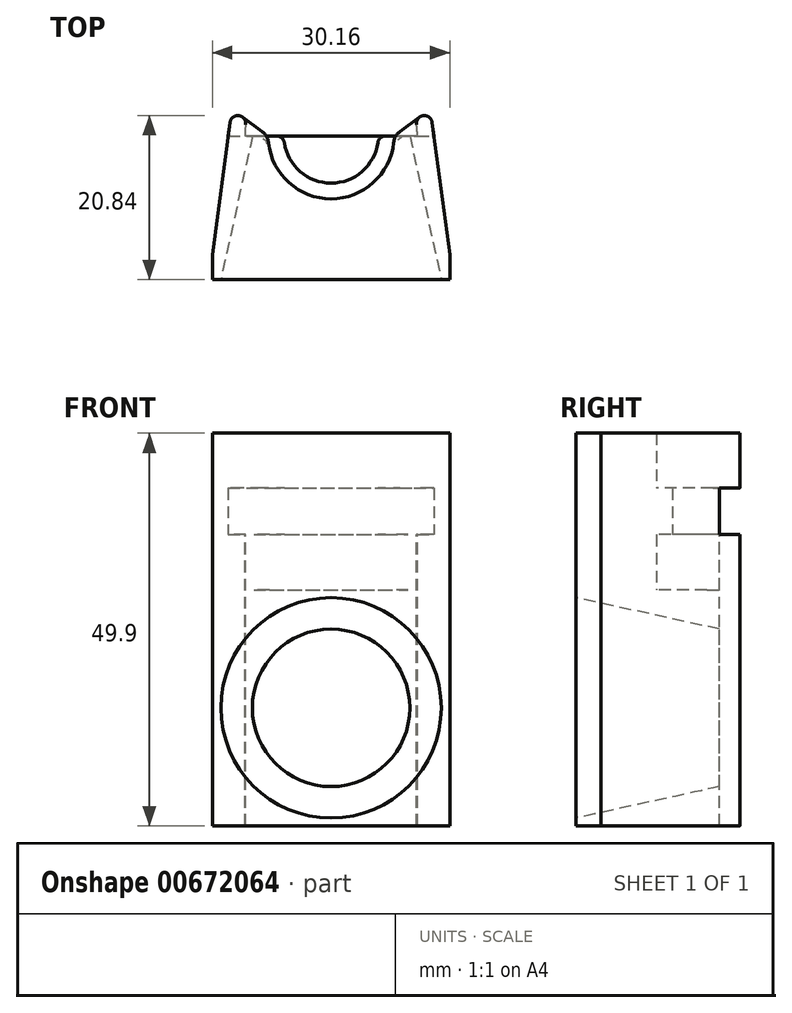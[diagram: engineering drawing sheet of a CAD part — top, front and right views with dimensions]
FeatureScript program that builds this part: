
annotation { "Feature Type Name" : "Feature", "Feature Type Description" : "" }
export const myFeature = defineFeature(function(context is Context, id is Id, definition is map)
    precondition{}
    {
        {
            var Q0;
            Q0=qCreatedBy(makeId("Top.planeOp"),FACE);
            var sketch = newSketch(context, id + "F0", { "sketchPlane" : qUnion([Q0])});
            skLineSegment(sketch, "E0.bottom", {"start": v(25.4, -25.4) * mm, "end": v(-25.4, -25.4) * mm});
            skLineSegment(sketch, "E0.top", {"start": v(25.4, 25.4) * mm, "end": v(-25.4, 25.4) * mm});
            skLineSegment(sketch, "E0.left", {"start": v(25.4, -25.4) * mm, "end": v(25.4, 25.4) * mm});
            skLineSegment(sketch, "E0.right", {"start": v(-25.4, -25.4) * mm, "end": v(-25.4, 25.4) * mm});
            skPoint(sketch, "E0.middle", {"position": v(0, 0) * mm});
            skSolve(sketch);
        }
        {
            var Q0;
            Q0 = qSketchRegion(id + "F0", true);
            extrude(context, id + "F1", {"entities" : qUnion([Q0]), "depth" : 30 * mm, "offsetDistance" : 25.4 * mm});
        }
        {
            var Q0;
            Q0=makeQuery(id+"F1.opExtrude","CAP_FACE",FACE,{"disambiguationData":[OSD([sQuery(id+"F0.wireOp",EDGE,"E0.bottom"),sQuery(id+"F0.wireOp",EDGE,"E0.top"),sQuery(id+"F0.wireOp",EDGE,"E0.left"),sQuery(id+"F0.wireOp",EDGE,"E0.right")])],"isStart":false});
            var sketch = newSketch(context, id + "F2", { "sketchPlane" : qUnion([Q0])});
            skArc(sketch, "E1", {"start": v(-10.86, 1.45) * mm, "mid": v(0, -10.95) * mm, "end": v(10.86, 1.45) * mm});
            skLineSegment(sketch, "E2.bottom", {"start": v(15.08, -15.08) * mm, "end": v(-15.08, -15.08) * mm});
            skLineSegment(sketch, "E3", {"start": v(-10.95, 0) * mm, "end": v(12.95, 0) * mm});
            skPoint(sketch, "E2.top.end.orphan", {"position": v(-15.08, 15.08) * mm});
            skPoint(sketch, "E4.orphan", {"position": v(15.08, 15.08) * mm});
            skPoint(sketch, "E5.orphan", {"position": v(15.08, 0) * mm});
            skPoint(sketch, "E2.right.end.orphan", {"position": v(-15.08, 0) * mm});
            skLineSegment(sketch, "E6.0", {"start": v(15.08, -18.26) * mm, "end": v(-15.08, -18.26) * mm});
            skLineSegment(sketch, "E7", {"start": v(-15.08, -15.08) * mm, "end": v(-15.08, -18.26) * mm});
            skLineSegment(sketch, "E8", {"start": v(15.08, -15.08) * mm, "end": v(15.08, -18.26) * mm});
            skLineSegment(sketch, "E9", {"start": v(15.08, -15.08) * mm, "end": v(12.84, 1.71) * mm});
            skLineSegment(sketch, "E10", {"start": v(-15.08, -15.08) * mm, "end": v(-12.84, 1.71) * mm});
            skArc(sketch, "E11", {"start": v(12.84, 1.71) * mm, "mid": v(11.72, 2.57) * mm, "end": v(10.86, 1.45) * mm});
            skArc(sketch, "E12", {"start": v(-10.86, 1.45) * mm, "mid": v(-11.72, 2.57) * mm, "end": v(-12.84, 1.71) * mm});
            skSolve(sketch);
        }
        {
            var Q0;
            Q0=makeQuery(id+"F2.imprint","IMPRINT",FACE,{"disambiguationData":[TD([[makeQuery(id+"F2.imprint","IMPRINT",EDGE,{"derivedFrom":sQuery(id+"F2.wireOp",EDGE,"E6.0")}),1.0]])]});
            var Q1;
            {var subQ0=sQuery(id+"F2.wireOp",EDGE,"E3");var subQ1=sQuery(id+"F2.wireOp",EDGE,"E1");var subQ2=makeQuery(id+"F2.imprint","INTERSECT",VERTEX,{"disambiguationData":[OD(0.0)],"derivedFrom":[subQ1,subQ0]});Q1=makeQuery(id+"F2.imprint","IMPRINT",FACE,{"disambiguationData":[TD([[makeQuery(id+"F2.imprint","IMPRINT",EDGE,{"disambiguationData":[TD([[subQ2,-1.0]])],"derivedFrom":subQ1}),1.0]])]});}
            var Q2;
            Q2=makeQuery(id+"F1.opExtrude","CAP_FACE",FACE,{"disambiguationData":[OSD([sQuery(id+"F0.wireOp",EDGE,"E0.bottom"),sQuery(id+"F0.wireOp",EDGE,"E0.top"),sQuery(id+"F0.wireOp",EDGE,"E0.left"),sQuery(id+"F0.wireOp",EDGE,"E0.right")])],"isStart":true});
            extrude(context, id + "F3", {"entities" : qUnion([Q0, Q1]), "operationType" : NewBodyOperationType.REMOVE, "endBound" : BoundingType.UP_TO_SURFACE, "oppositeDirection" : true, "depth" : 25.4 * mm, "endBoundEntityFace" : qUnion([Q2]), "offsetDistance" : 25.4 * mm});
        }
        {
            var Q0;
            Q0=makeQuery(id+"F3.boolean.opBoolean","COPY",FACE,{"derivedFrom":makeQuery(id+"F3.opExtrude","SWEPT_FACE",FACE,{"disambiguationData":[OSD([sQuery(id+"F2.wireOp",EDGE,"E6.0")])]})});
            var sketch = newSketch(context, id + "F4", { "sketchPlane" : qUnion([Q0])});
            skCircle(sketch, "E13", {"center": v(0, 15) * mm, "radius": 14 * mm});
            skSolve(sketch);
        }
        {
            var Q0;
            Q0=qCreatedBy(makeId("Front.planeOp"),FACE);
            var sketch = newSketch(context, id + "F5", { "sketchPlane" : qUnion([Q0])});
            skCircle(sketch, "E14", {"center": v(0, 15) * mm, "radius": 10 * mm});
            skSolve(sketch);
        }
        {
            var Q1;
            Q1=makeQuery(id+"F5.imprint","IMPRINT",FACE,{"disambiguationData":[TD([[makeQuery(id+"F5.imprint","IMPRINT",EDGE,{"derivedFrom":sQuery(id+"F5.wireOp",EDGE,"E14")}),1.0]])]});
            var Q2;
            Q2=makeQuery(id+"F4.imprint","IMPRINT",FACE,{"disambiguationData":[TD([[makeQuery(id+"F4.imprint","IMPRINT",EDGE,{"derivedFrom":sQuery(id+"F4.wireOp",EDGE,"E13")}),1.0]])]});
            var Q3;
            Q3=makeQuery(id+"F5.imprint","IMPRINT",FACE,{"disambiguationData":[TD([[makeQuery(id+"F5.imprint","IMPRINT",EDGE,{"derivedFrom":sQuery(id+"F5.wireOp",EDGE,"E14")}),1.0]])]});
            var Q4;
            Q4=makeQuery(id+"F4.imprint","IMPRINT",FACE,{"disambiguationData":[TD([[makeQuery(id+"F4.imprint","IMPRINT",EDGE,{"derivedFrom":sQuery(id+"F4.wireOp",EDGE,"E13")}),1.0]])]});
            loft(context, id + "F6", {"operationType" : NewBodyOperationType.REMOVE, "sheetProfilesArray" : [{ "sheetProfileEntities" : qUnion([Q1]) }, { "sheetProfileEntities" : qUnion([Q2]) }], "wireProfilesArray" : [{ "wireProfileEntities" : qUnion([Q3]) }, { "wireProfileEntities" : qUnion([Q4]) }]});
        }
        {
            var Q0;
            Q0=makeQuery(id+"F1.opExtrude","CAP_FACE",FACE,{"disambiguationData":[OSD([sQuery(id+"F0.wireOp",EDGE,"E0.bottom"),sQuery(id+"F0.wireOp",EDGE,"E0.top"),sQuery(id+"F0.wireOp",EDGE,"E0.left"),sQuery(id+"F0.wireOp",EDGE,"E0.right")])],"isStart":false});
            var sketch = newSketch(context, id + "F7", { "sketchPlane" : qUnion([Q0])});
            skArc(sketch, "E15", {"start": v(-8, 0) * mm, "mid": v(0, -8) * mm, "end": v(8, 0) * mm});
            skLineSegment(sketch, "E16", {"start": v(-8, 0) * mm, "end": v(-11.26, 2.39) * mm});
            skLineSegment(sketch, "E17", {"start": v(8, 0) * mm, "end": v(11.26, 2.39) * mm});
            skSolve(sketch);
        }
        {
            var Q0;
            {var subQ0=makeQuery(id+"F3.boolean.opBoolean","COPY",EDGE,{"derivedFrom":makeQuery(id+"F3.opExtrude","CAP_EDGE",EDGE,{"disambiguationData":[OSD([sQuery(id+"F2.wireOp",EDGE,"E1")])],"isStart":true})});Q0=makeQuery(id+"F7.imprint","IMPRINT",FACE,{"disambiguationData":[TD([[makeQuery(id+"F7.imprint","IMPRINT",EDGE,{"derivedFrom":subQ0}),-1.0]])]});}
            var Q1;
            Q1=makeQuery(id+"F7.imprint","IMPRINT",FACE,{"disambiguationData":[TD([[makeQuery(id+"F7.imprint","IMPRINT",EDGE,{"derivedFrom":sQuery(id+"F7.wireOp",EDGE,"E15")}),-1.0]])]});
            extrude(context, id + "F8", {"entities" : qUnion([Q0, Q1]), "operationType" : NewBodyOperationType.ADD, "depth" : 7 * mm, "offsetDistance" : 25.4 * mm});
        }
        {
            var Q0;
            Q0=makeQuery(id+"F8.opExtrude","CAP_FACE",FACE,{"disambiguationData":[OSD([sQuery(id+"F2.wireOp",EDGE,"E6.0"),sQuery(id+"F2.wireOp",EDGE,"E7"),sQuery(id+"F2.wireOp",EDGE,"E8"),sQuery(id+"F2.wireOp",EDGE,"E9"),sQuery(id+"F2.wireOp",EDGE,"E10"),sQuery(id+"F2.wireOp",EDGE,"E11"),sQuery(id+"F2.wireOp",EDGE,"E12"),sQuery(id+"F7.wireOp",EDGE,"E15"),sQuery(id+"F7.wireOp",EDGE,"E16"),sQuery(id+"F7.wireOp",EDGE,"E17")])],"isStart":false});
            var sketch = newSketch(context, id + "F9", { "sketchPlane" : qUnion([Q0])});
            skArc(sketch, "E18", {"start": v(-6, 0) * mm, "mid": v(0, -6) * mm, "end": v(6, 0) * mm});
            skLineSegment(sketch, "E19", {"start": v(-6, 0) * mm, "end": v(6, 0) * mm});
            skLineSegment(sketch, "E20", {"start": v(-6, 0) * mm, "end": v(-15.54, 0) * mm});
            skLineSegment(sketch, "E21", {"start": v(6, 0) * mm, "end": v(17.26, 0) * mm});
            skSolve(sketch);
        }
        {
            var Q0;
            {var subQ0=makeQuery(id+"F8.opExtrude","CAP_EDGE",EDGE,{"disambiguationData":[OSD([sQuery(id+"F7.wireOp",EDGE,"E15")])],"isStart":false});Q0=makeQuery(id+"F9.imprint","IMPRINT",FACE,{"disambiguationData":[TD([[makeQuery(id+"F9.imprint","IMPRINT",EDGE,{"derivedFrom":subQ0}),-1.0]])]});}
            var Q1;
            {var subQ0=sQuery(id+"F9.wireOp",EDGE,"E18");Q1=makeQuery(id+"F9.imprint","IMPRINT",FACE,{"disambiguationData":[TD([[makeQuery(id+"F9.imprint","IMPRINT",EDGE,{"derivedFrom":subQ0}),-1.0]])]});}
            extrude(context, id + "F10", {"entities" : qUnion([Q0, Q1]), "operationType" : NewBodyOperationType.ADD, "depth" : 5.9 * mm, "offsetDistance" : 25.4 * mm});
        }
        {
            var Q0;
            Q0=makeQuery(id+"F10.opExtrude","CAP_FACE",FACE,{"disambiguationData":[OSD([sQuery(id+"F2.wireOp",EDGE,"E6.0"),sQuery(id+"F2.wireOp",EDGE,"E7"),sQuery(id+"F2.wireOp",EDGE,"E8"),sQuery(id+"F2.wireOp",EDGE,"E9"),sQuery(id+"F2.wireOp",EDGE,"E10"),sQuery(id+"F9.wireOp",EDGE,"E18"),sQuery(id+"F9.wireOp",EDGE,"E20"),sQuery(id+"F9.wireOp",EDGE,"E21")])],"isStart":false});
            var sketch = newSketch(context, id + "F11", { "sketchPlane" : qUnion([Q0])});
            skArc(sketch, "E22", {"start": v(-8, 0) * mm, "mid": v(0, -8) * mm, "end": v(8, 0) * mm});
            skLineSegment(sketch, "E23", {"start": v(-8, 0) * mm, "end": v(8, 0) * mm});
            skPoint(sketch, "E24.orphan", {"position": v(15.08, 0) * mm});
            skPoint(sketch, "E25.right.end.orphan", {"position": v(-15.08, 0) * mm});
            skLineSegment(sketch, "E26.0", {"start": v(15.08, -18.26) * mm, "end": v(-15.08, -18.26) * mm});
            skLineSegment(sketch, "E27", {"start": v(-15.08, -15.08) * mm, "end": v(-15.08, -18.26) * mm});
            skLineSegment(sketch, "E28", {"start": v(15.08, -15.08) * mm, "end": v(15.08, -18.26) * mm});
            skLineSegment(sketch, "E29", {"start": v(15.08, -15.08) * mm, "end": v(12.84, 1.71) * mm});
            skLineSegment(sketch, "E30", {"start": v(-15.08, -15.08) * mm, "end": v(-12.84, 1.71) * mm});
            skArc(sketch, "E31", {"start": v(12.84, 1.71) * mm, "mid": v(12.24, 2.5) * mm, "end": v(11.26, 2.39) * mm});
            skArc(sketch, "E32", {"start": v(-11.26, 2.39) * mm, "mid": v(-12.24, 2.5) * mm, "end": v(-12.84, 1.71) * mm});
            skLineSegment(sketch, "E33", {"start": v(-8, 0) * mm, "end": v(-11.26, 2.39) * mm});
            skLineSegment(sketch, "E34", {"start": v(8, 0) * mm, "end": v(11.26, 2.39) * mm});
            skSolve(sketch);
        }
        {
            var Q0;
            {var subQ3=sQuery(id+"F11.wireOp",EDGE,"E31");Q0=makeQuery(id+"F11.imprint","IMPRINT",FACE,{"disambiguationData":[TD([[makeQuery(id+"F11.imprint","IMPRINT",EDGE,{"derivedFrom":subQ3}),1.0]])]});}
            var Q1;
            {var subQ3=sQuery(id+"F11.wireOp",EDGE,"E32");Q1=makeQuery(id+"F11.imprint","IMPRINT",FACE,{"disambiguationData":[TD([[makeQuery(id+"F11.imprint","IMPRINT",EDGE,{"derivedFrom":subQ3}),1.0]])]});}
            var Q2;
            {var subQ5=sQuery(id+"F11.wireOp",EDGE,"E22");Q2=makeQuery(id+"F11.imprint","IMPRINT",FACE,{"disambiguationData":[TD([[makeQuery(id+"F11.imprint","IMPRINT",EDGE,{"derivedFrom":subQ5}),-1.0]])]});}
            extrude(context, id + "F12", {"entities" : qUnion([Q0, Q1, Q2]), "operationType" : NewBodyOperationType.ADD, "depth" : 7 * mm, "offsetDistance" : 25.4 * mm});
        }
        {
            var Q0;
            Q0=makeQuery(id+"F12.opExtrude","SWEPT_EDGE",EDGE,{"disambiguationData":[OSD([sQuery(id+"F9.wireOp",EDGE,"E20"),sQuery(id+"F11.wireOp",EDGE,"E22"),sQuery(id+"F11.wireOp",EDGE,"E23"),sQuery(id+"F11.wireOp",EDGE,"E33")])]});
            var Q1;
            Q1=makeQuery(id+"F8.opExtrude","SWEPT_EDGE",EDGE,{"disambiguationData":[OSD([sQuery(id+"F7.wireOp",EDGE,"E15"),sQuery(id+"F7.wireOp",EDGE,"E16")])]});
            var Q2;
            Q2=makeQuery(id+"F12.opExtrude","SWEPT_EDGE",EDGE,{"disambiguationData":[OSD([sQuery(id+"F9.wireOp",EDGE,"E21"),sQuery(id+"F11.wireOp",EDGE,"E22"),sQuery(id+"F11.wireOp",EDGE,"E23"),sQuery(id+"F11.wireOp",EDGE,"E34")])]});
            var Q3;
            Q3=makeQuery(id+"F8.opExtrude","SWEPT_EDGE",EDGE,{"disambiguationData":[OSD([sQuery(id+"F7.wireOp",EDGE,"E15"),sQuery(id+"F7.wireOp",EDGE,"E17")])]});
            fillet(context, id + "F13", {"entities" : qUnion([Q0, Q1, Q2, Q3]), "radius" : 2 * mm, "tangentPropagation" : true, "allowEdgeOverflow" : false});
        }
        {
            var Q0;
            Q0=makeQuery(id+"F10.opExtrude","SWEPT_EDGE",EDGE,{"disambiguationData":[OSD([sQuery(id+"F9.wireOp",EDGE,"E18"),sQuery(id+"F9.wireOp",EDGE,"E19"),sQuery(id+"F9.wireOp",EDGE,"E20")])]});
            var Q1;
            Q1=makeQuery(id+"F10.opExtrude","SWEPT_EDGE",EDGE,{"disambiguationData":[OSD([sQuery(id+"F9.wireOp",EDGE,"E18"),sQuery(id+"F9.wireOp",EDGE,"E19"),sQuery(id+"F9.wireOp",EDGE,"E21")])]});
            fillet(context, id + "F14", {"entities" : qUnion([Q0, Q1]), "radius" : 1 * mm, "tangentPropagation" : true, "allowEdgeOverflow" : false});
        }
    });
